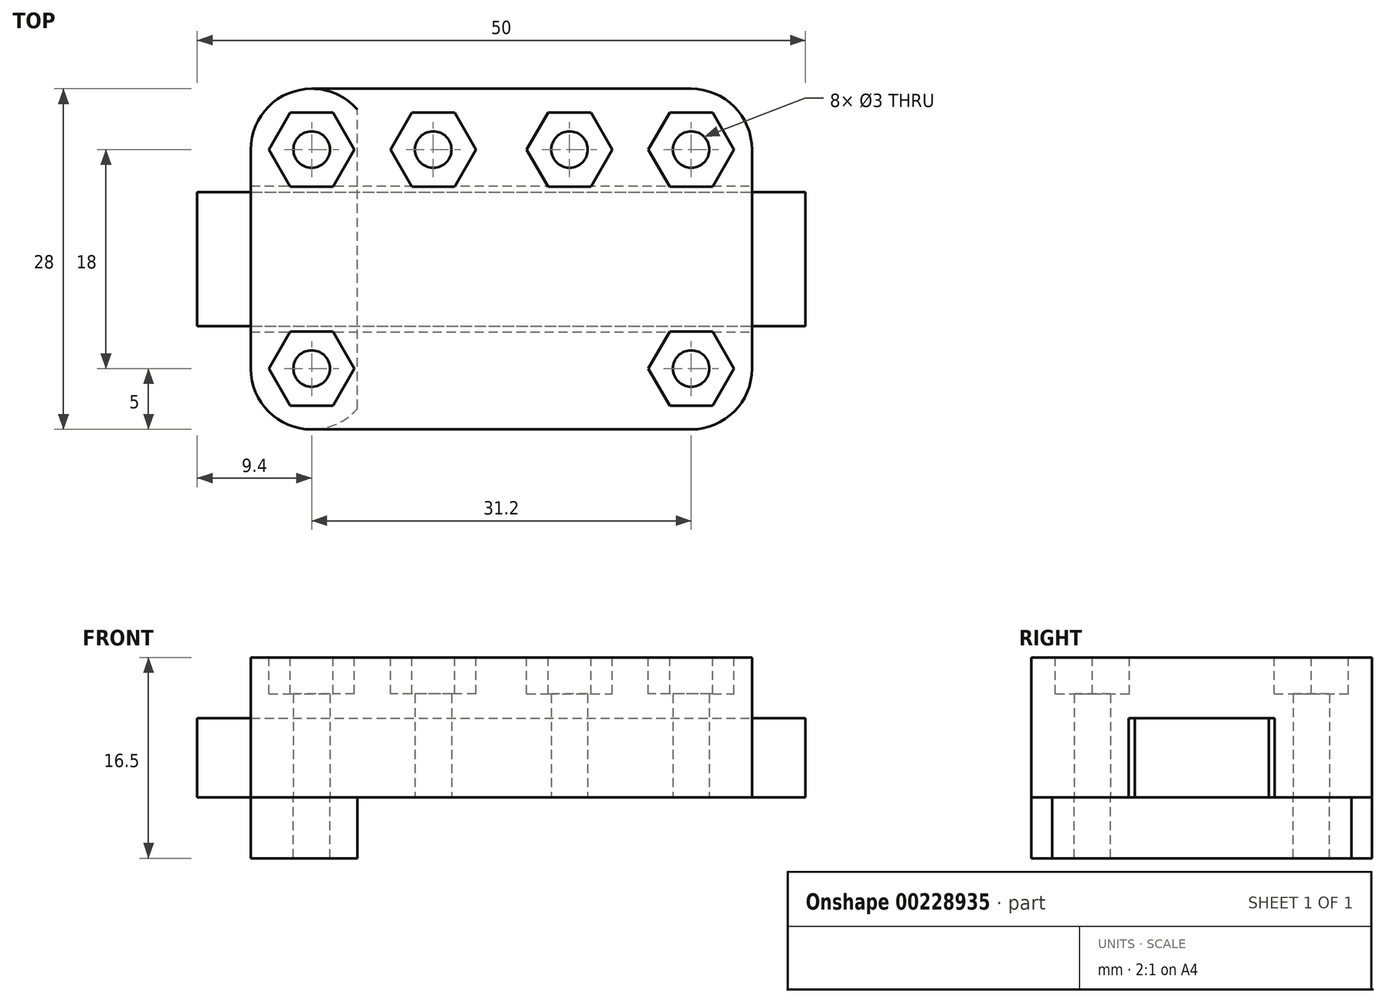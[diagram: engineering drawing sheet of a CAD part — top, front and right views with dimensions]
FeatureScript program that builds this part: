
annotation { "Feature Type Name" : "Feature", "Feature Type Description" : "" }
export const myFeature = defineFeature(function(context is Context, id is Id, definition is map)
    precondition{}
    {
        {
            var Q0;
            Q0=qCreatedBy(makeId("Top.planeOp"),FACE);
            var sketch = newSketch(context, id + "F0", { "sketchPlane" : qUnion([Q0])});
            skLineSegment(sketch, "E0.bottom", {"start": v(-25, 5.5) * mm, "end": v(25, 5.5) * mm});
            skLineSegment(sketch, "E0.top", {"start": v(-25, -5.5) * mm, "end": v(25, -5.5) * mm});
            skLineSegment(sketch, "E0.left", {"start": v(-25, 5.5) * mm, "end": v(-25, -5.5) * mm});
            skLineSegment(sketch, "E0.right", {"start": v(25, 5.5) * mm, "end": v(25, -5.5) * mm});
            skSolve(sketch);
        }
        {
            var Q0;
            Q0 = qSketchRegion(id + "F0", true);
            extrude(context, id + "F1", {"entities" : qUnion([Q0]), "depth" : 6.5 * mm});
        }
        {
            var Q0;
            Q0=qCreatedBy(makeId("Top.planeOp"),FACE);
            var sketch = newSketch(context, id + "F2", { "sketchPlane" : qUnion([Q0])});
            skCircle(sketch, "E1", {"center": v(-5.6, 9) * mm, "radius": 1.5 * mm});
            skCircle(sketch, "E2.MirrorC", {"center": v(5.6, 9) * mm, "radius": 1.5 * mm});
            skLineSegment(sketch, "E3", {"start": v(-10.6, 9) * mm, "end": v(-10.6, -14.56) * mm, "construction": true});
            skArc(sketch, "E4.filletArc", {"start": v(-5.6, 14) * mm, "mid": v(-9.14, 12.54) * mm, "end": v(-10.6, 9) * mm, "construction": true});
            skLineSegment(sketch, "E5", {"start": v(-5.6, 14) * mm, "end": v(0, 14) * mm, "construction": true});
            skLineSegment(sketch, "E6", {"start": v(0, 14) * mm, "end": v(-15.6, 14) * mm});
            skPoint(sketch, "E6.endSnap0", {"position": v(-2.8, 14) * mm});
            skCircle(sketch, "E7.MirrorC", {"center": v(-15.6, 9) * mm, "radius": 1.5 * mm});
            skLineSegment(sketch, "E8", {"start": v(-15.6, 9) * mm, "end": v(-15.6, 14) * mm, "construction": true});
            skArc(sketch, "E9", {"start": v(-15.6, 14) * mm, "mid": v(-19.14, 12.54) * mm, "end": v(-20.6, 9) * mm});
            skLineSegment(sketch, "E10", {"start": v(-15.6, 9) * mm, "end": v(-20.6, 9) * mm, "construction": true});
            skLineSegment(sketch, "E11", {"start": v(-20.6, 9) * mm, "end": v(-20.6, 6) * mm});
            skLineSegment(sketch, "E12", {"start": v(-20.6, 6) * mm, "end": v(0, 6) * mm});
            skLineSegment(sketch, "E13.MirrorCS", {"start": v(0, 14) * mm, "end": v(15.6, 14) * mm});
            skArc(sketch, "E14.MirrorCS", {"start": v(15.6, 14) * mm, "mid": v(19.14, 12.54) * mm, "end": v(20.6, 9) * mm});
            skLineSegment(sketch, "E15.MirrorCS", {"start": v(20.6, 9) * mm, "end": v(20.6, 6) * mm});
            skLineSegment(sketch, "E16.MirrorCS", {"start": v(20.6, 6) * mm, "end": v(0, 6) * mm});
            skCircle(sketch, "E17.MirrorC", {"center": v(15.6, 9) * mm, "radius": 1.5 * mm});
            skLineSegment(sketch, "E18.MirrorCS", {"start": v(-20.6, -6) * mm, "end": v(0, -6) * mm});
            skLineSegment(sketch, "E19.MirrorCS", {"start": v(-20.6, -9) * mm, "end": v(-20.6, -6) * mm});
            skArc(sketch, "E20.MirrorCS", {"start": v(-15.6, -14) * mm, "mid": v(-19.14, -12.54) * mm, "end": v(-20.6, -9) * mm});
            skLineSegment(sketch, "E21.MirrorCS", {"start": v(0, -14) * mm, "end": v(-15.6, -14) * mm});
            skLineSegment(sketch, "E22.MirrorCS", {"start": v(0, -14) * mm, "end": v(15.6, -14) * mm});
            skArc(sketch, "E23.MirrorCS", {"start": v(15.6, -14) * mm, "mid": v(19.14, -12.54) * mm, "end": v(20.6, -9) * mm});
            skLineSegment(sketch, "E24.MirrorCS", {"start": v(20.6, -9) * mm, "end": v(20.6, -6) * mm});
            skLineSegment(sketch, "E25.MirrorCS", {"start": v(20.6, -6) * mm, "end": v(0, -6) * mm});
            skCircle(sketch, "E26.MirrorC", {"center": v(-15.6, -9) * mm, "radius": 1.5 * mm});
            skCircle(sketch, "E27.MirrorC", {"center": v(15.6, -9) * mm, "radius": 1.5 * mm});
            skSolve(sketch);
        }
        {
            var Q0;
            Q0 = qSketchRegion(id + "F2", true);
            extrude(context, id + "F3", {"entities" : qUnion([Q0]), "depth" : 6.5 * mm});
        }
        {
            var Q0;
            Q0=makeQuery(id+"F3.opExtrude","CAP_FACE",FACE,{"disambiguationData":[OSD([sQuery(id+"F2.wireOp",EDGE,"E1"),sQuery(id+"F2.wireOp",EDGE,"E2.MirrorC"),sQuery(id+"F2.wireOp",EDGE,"E6"),sQuery(id+"F2.wireOp",EDGE,"E7.MirrorC"),sQuery(id+"F2.wireOp",EDGE,"E9"),sQuery(id+"F2.wireOp",EDGE,"E11"),sQuery(id+"F2.wireOp",EDGE,"E12"),sQuery(id+"F2.wireOp",EDGE,"E13.MirrorCS"),sQuery(id+"F2.wireOp",EDGE,"E14.MirrorCS"),sQuery(id+"F2.wireOp",EDGE,"E15.MirrorCS"),sQuery(id+"F2.wireOp",EDGE,"E16.MirrorCS"),sQuery(id+"F2.wireOp",EDGE,"E17.MirrorC")])],"isStart":false});
            var sketch = newSketch(context, id + "F4", { "sketchPlane" : qUnion([Q0])});
            skPoint(sketch, "E28.center.orphan", {"position": v(-15.6, 9) * mm});
            skCircle(sketch, "E29", {"center": v(-15.6, 9) * mm, "radius": 1.5 * mm});
            skLineSegment(sketch, "E30", {"start": v(0, 14) * mm, "end": v(-15.6, 14) * mm});
            skArc(sketch, "E31", {"start": v(-15.6, 14) * mm, "mid": v(-19.14, 12.54) * mm, "end": v(-20.6, 9) * mm});
            skLineSegment(sketch, "E32", {"start": v(0, 14) * mm, "end": v(0, -15.66) * mm, "construction": true});
            skLineSegment(sketch, "E33.MirrorCS", {"start": v(0, 14) * mm, "end": v(15.6, 14) * mm});
            skArc(sketch, "E34.MirrorCS", {"start": v(15.6, 14) * mm, "mid": v(19.14, 12.54) * mm, "end": v(20.6, 9) * mm});
            skLineSegment(sketch, "E35", {"start": v(-27.86, 0) * mm, "end": v(26.59, 0) * mm, "construction": true});
            skLineSegment(sketch, "E36.MirrorCS", {"start": v(0, -14) * mm, "end": v(-15.6, -14) * mm});
            skLineSegment(sketch, "E37.MirrorCS", {"start": v(0, -14) * mm, "end": v(15.6, -14) * mm});
            skArc(sketch, "E38.MirrorCS", {"start": v(-15.6, -14) * mm, "mid": v(-19.14, -12.54) * mm, "end": v(-20.6, -9) * mm});
            skArc(sketch, "E39.MirrorCS", {"start": v(15.6, -14) * mm, "mid": v(19.14, -12.54) * mm, "end": v(20.6, -9) * mm});
            skLineSegment(sketch, "E40", {"start": v(-20.6, 9) * mm, "end": v(-20.6, -9) * mm});
            skLineSegment(sketch, "E41", {"start": v(20.6, 9) * mm, "end": v(20.6, -9) * mm});
            skLineSegment(sketch, "E42.MirrorCS", {"start": v(27.86, 0) * mm, "end": v(-26.59, 0) * mm, "construction": true});
            skCircle(sketch, "E43.MirrorC", {"center": v(15.6, 9) * mm, "radius": 1.5 * mm});
            skCircle(sketch, "E44.MirrorC", {"center": v(-15.6, -9) * mm, "radius": 1.5 * mm});
            skCircle(sketch, "E45.MirrorC", {"center": v(15.6, -9) * mm, "radius": 1.5 * mm});
            skCircle(sketch, "E46", {"center": v(-5.6, 9) * mm, "radius": 1.5 * mm});
            skCircle(sketch, "E47.MirrorC", {"center": v(5.6, 9) * mm, "radius": 1.5 * mm});
            skSolve(sketch);
        }
        {
            var Q0;
            Q0 = qSketchRegion(id + "F4", true);
            extrude(context, id + "F5", {"entities" : qUnion([Q0]), "operationType" : NewBodyOperationType.ADD, "depth" : 5 * mm});
        }
        {
            var Q0;
            Q0=makeQuery(id+"F3.opExtrude","CAP_FACE",FACE,{"disambiguationData":[OSD([sQuery(id+"F2.wireOp",EDGE,"E18.MirrorCS"),sQuery(id+"F2.wireOp",EDGE,"E19.MirrorCS"),sQuery(id+"F2.wireOp",EDGE,"E20.MirrorCS"),sQuery(id+"F2.wireOp",EDGE,"E21.MirrorCS"),sQuery(id+"F2.wireOp",EDGE,"E22.MirrorCS"),sQuery(id+"F2.wireOp",EDGE,"E23.MirrorCS"),sQuery(id+"F2.wireOp",EDGE,"E24.MirrorCS"),sQuery(id+"F2.wireOp",EDGE,"E25.MirrorCS"),sQuery(id+"F2.wireOp",EDGE,"E26.MirrorC"),sQuery(id+"F2.wireOp",EDGE,"E27.MirrorC")])],"isStart":true});
            var sketch = newSketch(context, id + "F6", { "sketchPlane" : qUnion([Q0])});
            skLineSegment(sketch, "E48", {"start": v(-20.6, 9) * mm, "end": v(-20.6, 0) * mm});
            skArc(sketch, "E49", {"start": v(-15.6, 14) * mm, "mid": v(-19.14, 12.54) * mm, "end": v(-20.6, 9) * mm});
            skLineSegment(sketch, "E50", {"start": v(-15.6, 9) * mm, "end": v(-15.6, 0) * mm, "construction": true});
            skArc(sketch, "E51.MirrorCS", {"start": v(-15.6, 14) * mm, "mid": v(-13.54, 13.56) * mm, "end": v(-11.85, 12.3) * mm});
            skLineSegment(sketch, "E52.MirrorCS", {"start": v(-20.6, -9) * mm, "end": v(-20.6, 0) * mm});
            skArc(sketch, "E53.MirrorCS", {"start": v(-15.6, -14) * mm, "mid": v(-13.54, -13.56) * mm, "end": v(-11.85, -12.3) * mm});
            skArc(sketch, "E54.MirrorCS", {"start": v(-15.6, -14) * mm, "mid": v(-19.14, -12.54) * mm, "end": v(-20.6, -9) * mm});
            skCircle(sketch, "E55", {"center": v(-15.6, 9) * mm, "radius": 1.5 * mm});
            skCircle(sketch, "E56.MirrorC", {"center": v(-15.6, -9) * mm, "radius": 1.5 * mm});
            skLineSegment(sketch, "E57", {"start": v(-15.6, 9) * mm, "end": v(-10.6, 9) * mm, "construction": true});
            skLineSegment(sketch, "E58", {"start": v(-13.1, 9) * mm, "end": v(-10.6, 9) * mm, "construction": true});
            skLineSegment(sketch, "E59", {"start": v(-11.85, 9) * mm, "end": v(-11.85, 12.3) * mm});
            skLineSegment(sketch, "E60", {"start": v(-11.85, 9) * mm, "end": v(-11.85, -12.3) * mm});
            skPoint(sketch, "E61.MirrorCS.start.orphan", {"position": v(-10.6, 9) * mm});
            skSolve(sketch);
        }
        {
            var Q0;
            Q0 = qSketchRegion(id + "F6", true);
            extrude(context, id + "F7", {"entities" : qUnion([Q0]), "depth" : 5 * mm});
        }
        {
            var Q0;
            Q0=makeQuery(id+"F5.opExtrude","CAP_FACE",FACE,{"disambiguationData":[OSD([sQuery(id+"F4.wireOp",EDGE,"E29"),sQuery(id+"F4.wireOp",EDGE,"E30"),sQuery(id+"F4.wireOp",EDGE,"E31"),sQuery(id+"F4.wireOp",EDGE,"E33.MirrorCS"),sQuery(id+"F4.wireOp",EDGE,"E34.MirrorCS"),sQuery(id+"F4.wireOp",EDGE,"E36.MirrorCS"),sQuery(id+"F4.wireOp",EDGE,"E37.MirrorCS"),sQuery(id+"F4.wireOp",EDGE,"E38.MirrorCS"),sQuery(id+"F4.wireOp",EDGE,"E39.MirrorCS"),sQuery(id+"F4.wireOp",EDGE,"E40"),sQuery(id+"F4.wireOp",EDGE,"E41"),sQuery(id+"F4.wireOp",EDGE,"E43.MirrorC"),sQuery(id+"F4.wireOp",EDGE,"E44.MirrorC"),sQuery(id+"F4.wireOp",EDGE,"E45.MirrorC"),sQuery(id+"F4.wireOp",EDGE,"E46"),sQuery(id+"F4.wireOp",EDGE,"E47.MirrorC")])],"isStart":false});
            var sketch = newSketch(context, id + "F8", { "sketchPlane" : qUnion([Q0])});
            skCircle(sketch, "E62.cCircle", {"center": v(-15.6, 9) * mm, "radius": 3.05 * mm, "construction": true});
            skLineSegment(sketch, "E62.0", {"start": v(-17.36, 12.05) * mm, "end": v(-13.84, 12.05) * mm});
            skLineSegment(sketch, "E62.1", {"start": v(-13.84, 12.05) * mm, "end": v(-12.08, 9) * mm});
            skLineSegment(sketch, "E62.2", {"start": v(-12.08, 9) * mm, "end": v(-13.84, 5.95) * mm});
            skLineSegment(sketch, "E62.3", {"start": v(-13.84, 5.95) * mm, "end": v(-17.36, 5.95) * mm});
            skLineSegment(sketch, "E62.4", {"start": v(-17.36, 5.95) * mm, "end": v(-19.12, 9) * mm});
            skLineSegment(sketch, "E62.5", {"start": v(-19.12, 9) * mm, "end": v(-17.36, 12.05) * mm});
            skPoint(sketch, "E62.0.midPoint", {"position": v(-15.6, 12.05) * mm});
            skLineSegment(sketch, "E63.MirrorCS", {"start": v(19.12, 9) * mm, "end": v(17.36, 12.05) * mm});
            skLineSegment(sketch, "E64.MirrorCS", {"start": v(17.36, 12.05) * mm, "end": v(13.84, 12.05) * mm});
            skLineSegment(sketch, "E65.MirrorCS", {"start": v(17.36, 5.95) * mm, "end": v(19.12, 9) * mm});
            skLineSegment(sketch, "E66.MirrorCS", {"start": v(13.84, 5.95) * mm, "end": v(17.36, 5.95) * mm});
            skLineSegment(sketch, "E67.MirrorCS", {"start": v(12.08, 9) * mm, "end": v(13.84, 5.95) * mm});
            skPoint(sketch, "E68.MirrorP", {"position": v(15.6, 12.05) * mm});
            skCircle(sketch, "E69.MirrorC", {"center": v(15.6, 9) * mm, "radius": 3.05 * mm, "construction": true});
            skLineSegment(sketch, "E70.MirrorCS", {"start": v(13.84, 12.05) * mm, "end": v(12.08, 9) * mm});
            skLineSegment(sketch, "E71.MirrorCS", {"start": v(-17.36, -12.05) * mm, "end": v(-13.84, -12.05) * mm});
            skLineSegment(sketch, "E72.MirrorCS", {"start": v(-12.08, -9) * mm, "end": v(-13.84, -5.95) * mm});
            skLineSegment(sketch, "E73.MirrorCS", {"start": v(-17.36, -5.95) * mm, "end": v(-19.12, -9) * mm});
            skPoint(sketch, "E74.MirrorP", {"position": v(-15.6, -12.05) * mm});
            skCircle(sketch, "E75.MirrorC", {"center": v(-15.6, -9) * mm, "radius": 3.05 * mm, "construction": true});
            skLineSegment(sketch, "E76.MirrorCS", {"start": v(-13.84, -12.05) * mm, "end": v(-12.08, -9) * mm});
            skLineSegment(sketch, "E77.MirrorCS", {"start": v(-13.84, -5.95) * mm, "end": v(-17.36, -5.95) * mm});
            skLineSegment(sketch, "E78.MirrorCS", {"start": v(-19.12, -9) * mm, "end": v(-17.36, -12.05) * mm});
            skLineSegment(sketch, "E79.MirrorCS", {"start": v(17.36, -12.05) * mm, "end": v(13.84, -12.05) * mm});
            skLineSegment(sketch, "E80.MirrorCS", {"start": v(12.08, -9) * mm, "end": v(13.84, -5.95) * mm});
            skLineSegment(sketch, "E81.MirrorCS", {"start": v(17.36, -5.95) * mm, "end": v(19.12, -9) * mm});
            skLineSegment(sketch, "E82.MirrorCS", {"start": v(13.84, -5.95) * mm, "end": v(17.36, -5.95) * mm});
            skPoint(sketch, "E83.MirrorP", {"position": v(15.6, -12.05) * mm});
            skCircle(sketch, "E84.MirrorC", {"center": v(15.6, -9) * mm, "radius": 3.05 * mm, "construction": true});
            skLineSegment(sketch, "E85.MirrorCS", {"start": v(19.12, -9) * mm, "end": v(17.36, -12.05) * mm});
            skLineSegment(sketch, "E86.MirrorCS", {"start": v(13.84, -12.05) * mm, "end": v(12.08, -9) * mm});
            skLineSegment(sketch, "E87", {"start": v(-15.6, 9) * mm, "end": v(-5.6, 9) * mm, "construction": true});
            skLineSegment(sketch, "E88", {"start": v(-10.6, 9) * mm, "end": v(-10.6, 4.66) * mm, "construction": true});
            skLineSegment(sketch, "E89.MirrorCS", {"start": v(-3.84, 12.05) * mm, "end": v(-7.36, 12.05) * mm});
            skLineSegment(sketch, "E90.MirrorCS", {"start": v(-7.36, 12.05) * mm, "end": v(-9.12, 9) * mm});
            skLineSegment(sketch, "E91.MirrorCS", {"start": v(-9.12, 9) * mm, "end": v(-7.36, 5.95) * mm});
            skPoint(sketch, "E92.MirrorP", {"position": v(-5.6, 12.05) * mm});
            skLineSegment(sketch, "E93.MirrorCS", {"start": v(-7.36, 5.95) * mm, "end": v(-3.84, 5.95) * mm});
            skLineSegment(sketch, "E94.MirrorCS", {"start": v(-3.84, 5.95) * mm, "end": v(-2.08, 9) * mm});
            skLineSegment(sketch, "E95.MirrorCS", {"start": v(-2.08, 9) * mm, "end": v(-3.84, 12.05) * mm});
            skCircle(sketch, "E96.MirrorC", {"center": v(-5.6, 9) * mm, "radius": 3.05 * mm, "construction": true});
            skLineSegment(sketch, "E97.MirrorCS", {"start": v(7.36, 5.95) * mm, "end": v(3.84, 5.95) * mm});
            skLineSegment(sketch, "E98.MirrorCS", {"start": v(3.84, 12.05) * mm, "end": v(7.36, 12.05) * mm});
            skLineSegment(sketch, "E99.MirrorCS", {"start": v(3.84, 5.95) * mm, "end": v(2.08, 9) * mm});
            skPoint(sketch, "E100.MirrorP", {"position": v(5.6, 12.05) * mm});
            skLineSegment(sketch, "E101.MirrorCS", {"start": v(7.36, 12.05) * mm, "end": v(9.12, 9) * mm});
            skCircle(sketch, "E102.MirrorC", {"center": v(5.6, 9) * mm, "radius": 3.05 * mm, "construction": true});
            skLineSegment(sketch, "E103.MirrorCS", {"start": v(9.12, 9) * mm, "end": v(7.36, 5.95) * mm});
            skLineSegment(sketch, "E104.MirrorCS", {"start": v(2.08, 9) * mm, "end": v(3.84, 12.05) * mm});
            skSolve(sketch);
        }
        {
            var Q0;
            Q0 = qSketchRegion(id + "F8", true);
            extrude(context, id + "F9", {"entities" : qUnion([Q0]), "operationType" : NewBodyOperationType.REMOVE, "oppositeDirection" : true, "depth" : 3 * mm});
        }
    });
